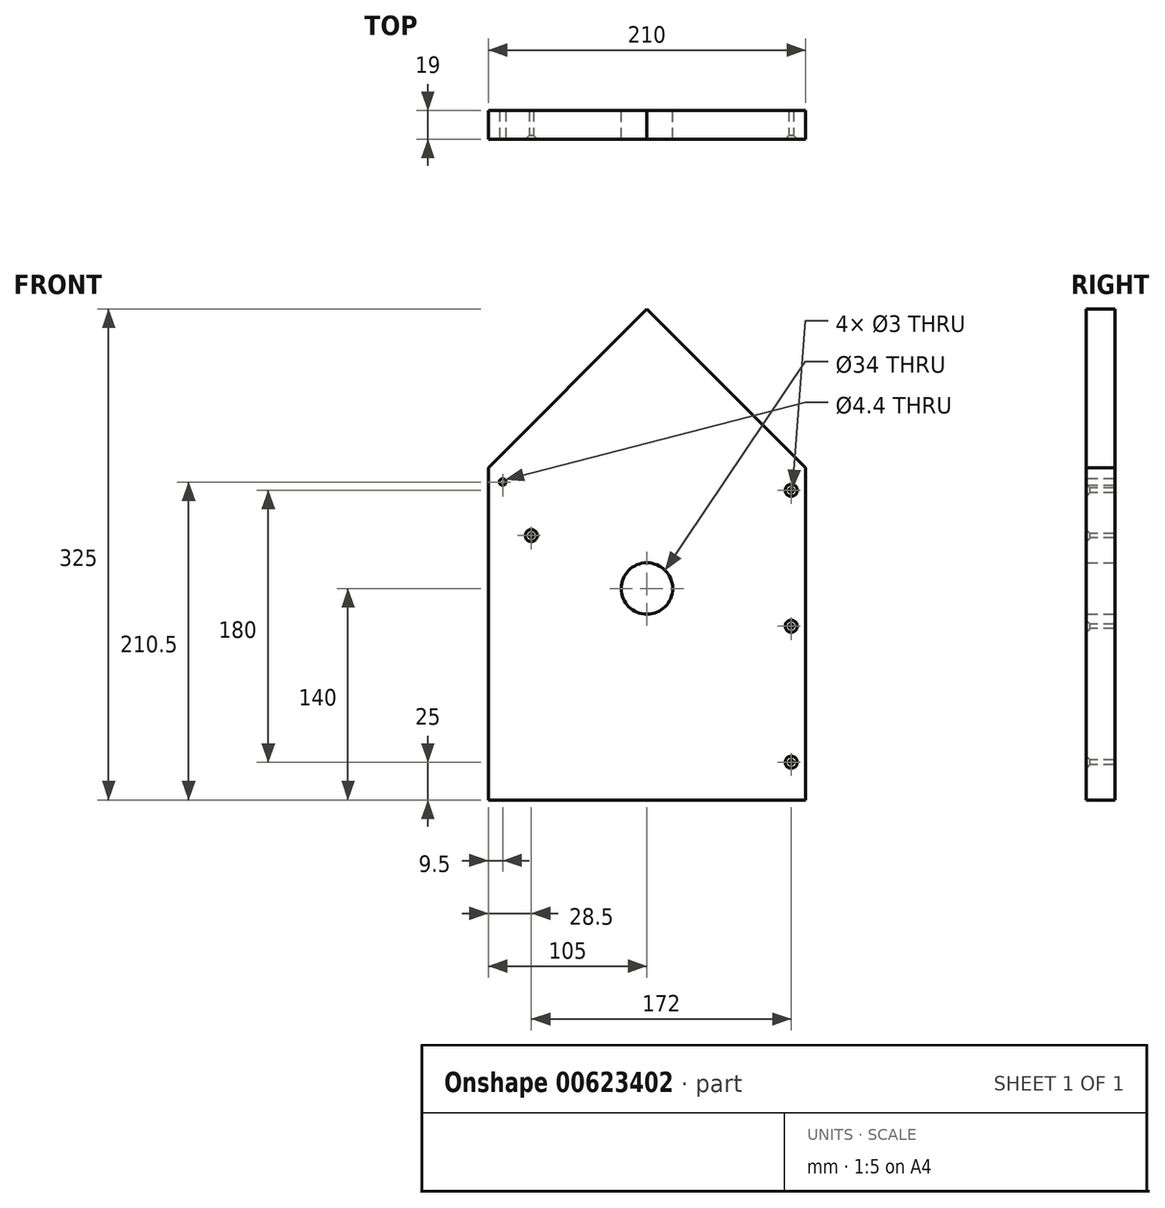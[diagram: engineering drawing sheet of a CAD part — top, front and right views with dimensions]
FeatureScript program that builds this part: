
annotation { "Feature Type Name" : "Feature", "Feature Type Description" : "" }
export const myFeature = defineFeature(function(context is Context, id is Id, definition is map)
    precondition{}
    {
        {
            var Q0;
            Q0=qCreatedBy(makeId("Top.planeOp"),FACE);
            var sketch = newSketch(context, id + "F0", { "sketchPlane" : qUnion([Q0])});
            skLineSegment(sketch, "E0", {"start": v(-50, 0) * mm, "end": v(50, 0) * mm, "construction": true});
            skLineSegment(sketch, "E1", {"start": v(0, 50) * mm, "end": v(0, -50) * mm, "construction": true});
            skSolve(sketch);
        }
        {
            var Q0;
            Q0=qCreatedBy(makeId("Front.planeOp"),FACE);
            var sketch = newSketch(context, id + "F1", { "sketchPlane" : qUnion([Q0])});
            skLineSegment(sketch, "E2", {"start": v(105, 220) * mm, "end": v(0, 325) * mm});
            skLineSegment(sketch, "E3.MirrorCS", {"start": v(-105, 220) * mm, "end": v(0, 325) * mm});
            skLineSegment(sketch, "E4", {"start": v(-105, 220) * mm, "end": v(-105, 0) * mm});
            skLineSegment(sketch, "E5", {"start": v(-105, 0) * mm, "end": v(105, 0) * mm});
            skLineSegment(sketch, "E6", {"start": v(105, 0) * mm, "end": v(105, 220) * mm});
            skCircle(sketch, "E7", {"center": v(0, 140) * mm, "radius": 17 * mm});
            skSolve(sketch);
        }
        {
            var Q0;
            Q0 = qSketchRegion(id + "F1", true);
            extrude(context, id + "F2", {"entities" : qUnion([Q0]), "depth" : 19 * mm, "offsetDistance" : 25 * mm});
        }
        {
            var Q0;
            Q0=makeQuery(id+"F2.opExtrude","CAP_FACE",FACE,{"disambiguationData":[OSD([sQuery(id+"F1.wireOp",EDGE,"E2"),sQuery(id+"F1.wireOp",EDGE,"E3.MirrorCS"),sQuery(id+"F1.wireOp",EDGE,"E4"),sQuery(id+"F1.wireOp",EDGE,"E5"),sQuery(id+"F1.wireOp",EDGE,"E6"),sQuery(id+"F1.wireOp",EDGE,"E7")])],"isStart":false});
            var sketch = newSketch(context, id + "F3", { "sketchPlane" : qUnion([Q0])});
            skPoint(sketch, "E8", {"position": v(95.5, 25) * mm});
            skPoint(sketch, "E9", {"position": v(95.5, 115) * mm});
            skPoint(sketch, "E10", {"position": v(95.5, 205) * mm});
            skPoint(sketch, "E11", {"position": v(-95.5, 210.5) * mm});
            skLineSegment(sketch, "E12", {"start": v(95.5, 205) * mm, "end": v(95.5, 115) * mm, "construction": true});
            skLineSegment(sketch, "E13", {"start": v(95.5, 115) * mm, "end": v(95.5, 25) * mm, "construction": true});
            skPoint(sketch, "E14", {"position": v(-76.5, 175) * mm});
            skSolve(sketch);
        }
        {
            var Q0;
            Q0=sQuery(id+"F3.wireOp",VERTEX,"E8");
            var Q1;
            Q1=sQuery(id+"F3.wireOp",VERTEX,"E9");
            var Q2;
            Q2=sQuery(id+"F3.wireOp",VERTEX,"E10");
            var Q3;
            Q3=sQuery(id+"F3.wireOp",VERTEX,"E14");
            var Q4;
            Q4=makeQuery(id+"F2.opExtrude","SWEPT_BODY",BODY,{"disambiguationData":[OSD([sQuery(id+"F1.wireOp",EDGE,"E2"),sQuery(id+"F1.wireOp",EDGE,"E3.MirrorCS"),sQuery(id+"F1.wireOp",EDGE,"E4"),sQuery(id+"F1.wireOp",EDGE,"E5"),sQuery(id+"F1.wireOp",EDGE,"E6"),sQuery(id+"F1.wireOp",EDGE,"E7")])]});
            hole(context, id + "F4", {"style" : HoleStyle.C_SINK, "endStyle" : HoleEndStyle.THROUGH, "holeDiameter" : 3 * mm, "cSinkDiameter" : 8 * mm, "cSinkAngle" : 90 * degree, "majorDiameter" : 5 * mm, "isTappedThrough" : true, "tappedDepth" : 12 * mm, "tapClearance" : 3, "startFromSketch" : true, "locations" : qUnion([Q0, Q1, Q2, Q3]), "scope" : qUnion([Q4])});
        }
        {
            var Q0;
            Q0=sQuery(id+"F3.wireOp",VERTEX,"E11");
            var Q1;
            Q1=makeQuery(id+"F2.opExtrude","SWEPT_BODY",BODY,{"disambiguationData":[OSD([sQuery(id+"F1.wireOp",EDGE,"E2"),sQuery(id+"F1.wireOp",EDGE,"E3.MirrorCS"),sQuery(id+"F1.wireOp",EDGE,"E4"),sQuery(id+"F1.wireOp",EDGE,"E5"),sQuery(id+"F1.wireOp",EDGE,"E6"),sQuery(id+"F1.wireOp",EDGE,"E7")])]});
            hole(context, id + "F5", {"style" : HoleStyle.SIMPLE, "endStyle" : HoleEndStyle.THROUGH, "standardTappedOrClearance" : lookupTablePath({ "standard" : "ISO", "fit" : "Normal", "size" : "M4", "type" : "Clearance" }), "standardBlindInLast" : lookupTablePath({ "fit" : "Standard", "standard" : "ISO", "size" : "M4", "type" : "Clearance" }), "holeDiameter" : 4.4 * mm, "majorDiameter" : 5 * mm, "isTappedThrough" : true, "tappedDepth" : 12 * mm, "tapClearance" : 3, "startFromSketch" : true, "locations" : qUnion([Q0]), "scope" : qUnion([Q1])});
        }
    });
